# Revit family: Water Cooled_VRF_Outdoor_8-10-12HP - 380V
name_source: partatom
category: Equipamento mecânico
units: mm (PartAtom-declared; Revit-internal decimal feet)

## family parameters
Com base no plano de trabalho = Não
Compartilhado = Não
Corte com vazios quando carregada = Não
Cota do conector redondo = Usar raio
Número OmniClass = 23.75.00.00
Ponto de cálculo do ambiente = Não
Sempre na vertical = Sim
Tipo de parte = Normal
Título OmniClass = Climate Control (HVAC)

## types (3) — shared parameters
Casing color = PANTONE warm gray 2c
Compressor = 1
Condensation = Water
Depth = 550
Descrição = High efficiency water cooled
Fabricante = TRANE
Gas = R410A
Height = 1000  [stored 3.28084 ft]
Installation = Outdoor installation
Power supply = 380-415V 3N~60Hz
Series = TVR II
Width = 780  [stored 2.55906 ft]
clearance access behind = 900  [stored 2.95276 ft]
clearance access front = 900  [stored 2.95276 ft]
clearance access left = 100  [stored 0.328084 ft]
clearance access right = 100  [stored 0.328084 ft]

## per-type parameters (varying)
| type | Cooling Capacity | Cooling Power Input | Gas pipe | Gas pipe radius | Heating Capacity | Heating Power Input | Liquid pipe | Liquid pipe radius | Maximum Fuse Amps | Minimum Circuit Amps | Net Weight | Rated water flow volume |
| 4TWH0086BK | 25.20 kW | 4.80 kW | 25.4  [stored 0.0833333 ft] | 12.7  [stored 0.0416667 ft] | 27.00 kW | 4.45 kW | 12.7  [stored 0.0416667 ft] | 6.35  [stored 0.0208333 ft] | 20 A | 19 A | 146.00 kg | 5.400 m³/h |
| 4TWH0096BK | 28.00 kW | 6.10 kW | 25.4  [stored 0.0833333 ft] | 12.7  [stored 0.0416667 ft] | 31.50 kW | 5.83 kW | 12.7  [stored 0.0416667 ft] | 6.35  [stored 0.0208333 ft] | 20 A | 19 A | 146.00 kg | 6.000 m³/h |
| 4TWH0115BK | 33.50 kW | 8.00 kW | 31.8  [stored 0.104331 ft] | 15.9  [stored 0.0521654 ft] | 37.50 kW | 7.80 kW | 15.9  [stored 0.0521654 ft] | 7.95  [stored 0.0260827 ft] | 25 A | 21 A | 147.00 kg | 7.200 m³/h |

note: column(s) folded — value = type name in every type: Modelo

note: [stored X ft] marks values corroborated as IEEE doubles in the binary element streams (Revit-internal decimal feet)

## geometry (parser evidence)
native form markers: Blend x4, Sweep x13
no freeform markers — native parametric forms only
